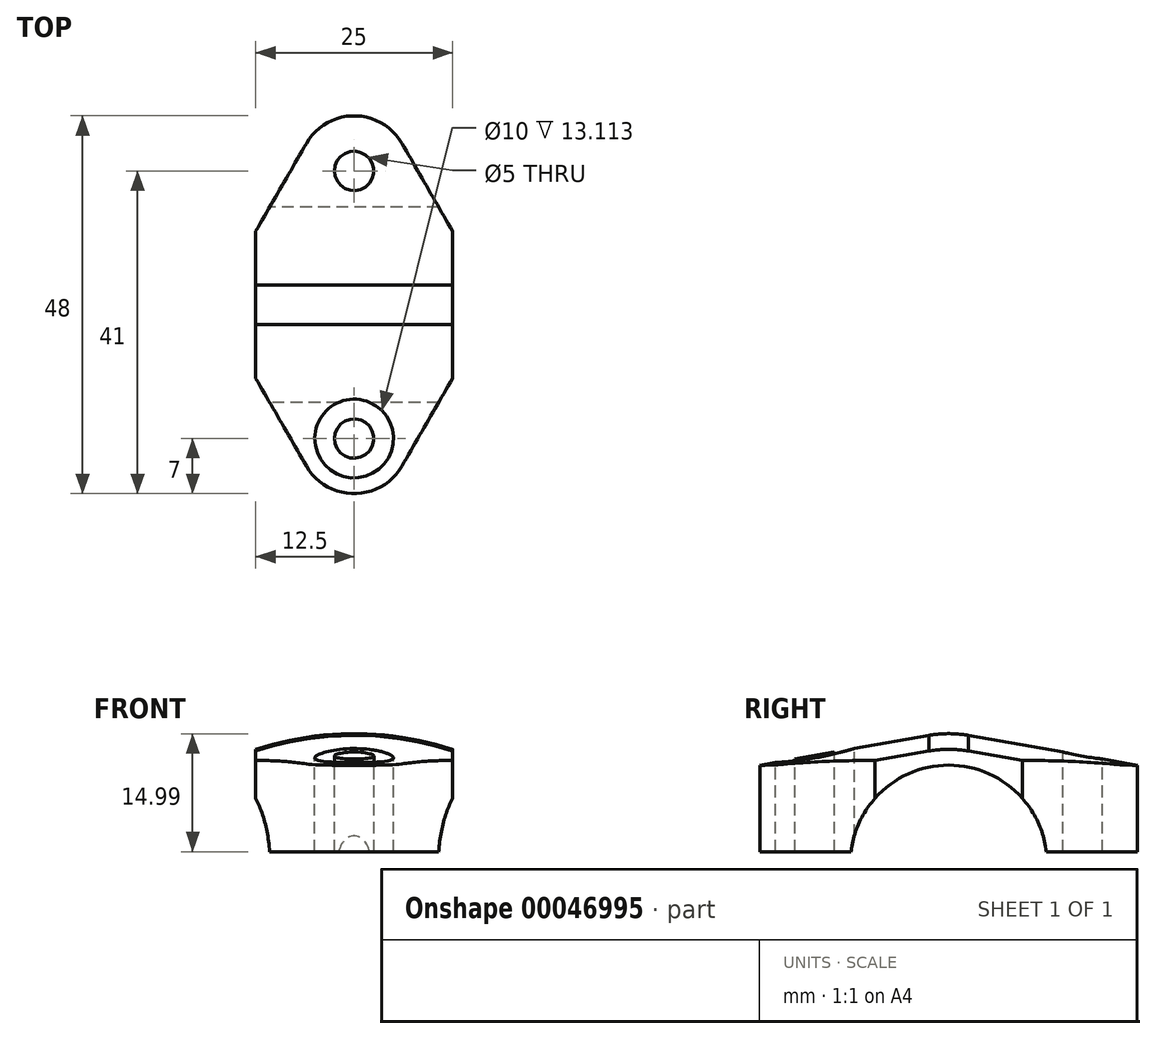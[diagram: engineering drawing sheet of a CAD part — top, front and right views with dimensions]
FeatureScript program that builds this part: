
annotation { "Feature Type Name" : "Feature", "Feature Type Description" : "" }
export const myFeature = defineFeature(function(context is Context, id is Id, definition is map)
    precondition{}
    {
        {
            var Q0;
            Q0=qCreatedBy(makeId("Right.planeOp"),FACE);
            var sketch = newSketch(context, id + "F0", { "sketchPlane" : qUnion([Q0])});
            skCircle(sketch, "E0", {"center": v(0, 0) * mm, "radius": 12.5 * mm});
            skCircle(sketch, "E1", {"center": v(0, 0) * mm, "radius": 14.5 * mm});
            skLineSegment(sketch, "E2", {"start": v(-78.22, 0) * mm, "end": v(73.33, 0) * mm, "construction": true});
            skLineSegment(sketch, "E3", {"start": v(-24, 1.5) * mm, "end": v(0, 1.5) * mm});
            skLineSegment(sketch, "E4", {"start": v(-2.52, 14.28) * mm, "end": v(-24, 10.5) * mm});
            skLineSegment(sketch, "E5", {"start": v(-24, 10.5) * mm, "end": v(-24, 1.5) * mm});
            skLineSegment(sketch, "E6", {"start": v(0, 19.52) * mm, "end": v(0, -21.8) * mm, "construction": true});
            skLineSegment(sketch, "E7.MirrorCS", {"start": v(24, 1.5) * mm, "end": v(0, 1.5) * mm});
            skLineSegment(sketch, "E8.MirrorCS", {"start": v(24, 10.5) * mm, "end": v(24, 1.5) * mm});
            skLineSegment(sketch, "E9.MirrorCS", {"start": v(2.52, 14.28) * mm, "end": v(24, 10.5) * mm});
            skSolve(sketch);
        }
        {
            var Q0;
            {var subQ0=sQuery(id+"F0.wireOp",EDGE,"E4");Q0=makeQuery(id+"F0.imprint","IMPRINT",FACE,{"disambiguationData":[TD([[makeQuery(id+"F0.imprint","IMPRINT",EDGE,{"derivedFrom":subQ0}),1.0]])]});}
            var Q1;
            {var subQ4=sQuery(id+"F0.wireOp",EDGE,"E8.MirrorCS");Q1=makeQuery(id+"F0.imprint","IMPRINT",FACE,{"disambiguationData":[TD([[makeQuery(id+"F0.imprint","IMPRINT",EDGE,{"derivedFrom":subQ4}),-1.0]])]});}
            var Q2;
            {var subQ2=sQuery(id+"F0.wireOp",EDGE,"E3");var subQ7=sQuery(id+"F0.wireOp",EDGE,"E0");var subQ8=makeQuery(id+"F0.imprint","INTERSECT",VERTEX,{"derivedFrom":[subQ7,subQ2]});Q2=makeQuery(id+"F0.imprint","IMPRINT",FACE,{"disambiguationData":[TD([[makeQuery(id+"F0.imprint","IMPRINT",EDGE,{"disambiguationData":[TD([[subQ8,1.0]])],"derivedFrom":subQ7}),-1.0]])]});}
            extrude(context, id + "F1", {"entities" : qUnion([Q0, Q1, Q2]), "endBound" : BoundingType.SYMMETRIC, "depth" : 25 * mm});
        }
        {
            var Q0;
            Q0=makeQuery(id+"F1.opExtrude","SWEPT_FACE",FACE,{"disambiguationData":[OSD([sQuery(id+"F0.wireOp",EDGE,"E5")])]});
            var sketch = newSketch(context, id + "F2", { "sketchPlane" : qUnion([Q0])});
            skArc(sketch, "E10", {"start": v(12.5, 10.5) * mm, "mid": v(0, 12.5) * mm, "end": v(-12.5, 10.5) * mm});
            skSolve(sketch);
        }
        {
            var Q0;
            Q0=makeQuery(id+"F2.imprint","IMPRINT",FACE,{"disambiguationData":[TD([[makeQuery(id+"F2.imprint","IMPRINT",EDGE,{"derivedFrom":sQuery(id+"F2.wireOp",EDGE,"E10")}),1.0]])]});
            var Q1;
            Q1=makeQuery(id+"F1.opExtrude","CAP_EDGE",EDGE,{"disambiguationData":[OSD([sQuery(id+"F0.wireOp",EDGE,"E4")])],"isStart":false});
            var Q2;
            Q2=makeQuery(id+"F1.opExtrude","CAP_EDGE",EDGE,{"disambiguationData":[OSD([sQuery(id+"F0.wireOp",EDGE,"E1")])],"isStart":false});
            var Q3;
            Q3=makeQuery(id+"F1.opExtrude","CAP_EDGE",EDGE,{"disambiguationData":[OSD([sQuery(id+"F0.wireOp",EDGE,"E9.MirrorCS")])],"isStart":false});
            sweep(context, id + "F3", {"operationType" : NewBodyOperationType.ADD, "profiles" : qUnion([Q0]), "path" : qUnion([Q1, Q2, Q3]), "keepProfileOrientation" : true});
        }
        {
            var Q0;
            Q0=makeQuery(id+"F1.opExtrude","SWEPT_FACE",FACE,{"disambiguationData":[OSD([sQuery(id+"F0.wireOp",EDGE,"E3")])]});
            cPlane(context, id + "F4", {"entities" : qUnion([Q0]), "cplaneType" : CPlaneType.OFFSET, "offset" : 30 * mm, "oppositeDirection" : true, "width" : 150 * mm, "height" : 150 * mm});
        }
        {
            var Q0;
            Q0=qCreatedBy(id+"F4.planeOp",FACE);
            var sketch = newSketch(context, id + "F5", { "sketchPlane" : qUnion([Q0])});
            skCircle(sketch, "E11", {"center": v(0, -17) * mm, "radius": 7 * mm});
            skLineSegment(sketch, "E12", {"start": v(-31.34, 0) * mm, "end": v(29.18, 0) * mm, "construction": true});
            skCircle(sketch, "E13", {"center": v(0, -17) * mm, "radius": 5 * mm});
            skCircle(sketch, "E14", {"center": v(0, -17) * mm, "radius": 2.5 * mm});
            skLineSegment(sketch, "E15", {"start": v(12.5, 24) * mm, "end": v(12.5, -24) * mm});
            skLineSegment(sketch, "E16", {"start": v(-12.5, -24) * mm, "end": v(-12.5, 24) * mm});
            skLineSegment(sketch, "E17", {"start": v(-6.06, -20.5) * mm, "end": v(-12.5, -9.35) * mm});
            skLineSegment(sketch, "E18", {"start": v(6.06, -20.5) * mm, "end": v(12.5, -9.35) * mm});
            skLineSegment(sketch, "E19", {"start": v(-12.5, -24) * mm, "end": v(12.5, -24) * mm});
            skLineSegment(sketch, "E20.MirrorCS", {"start": v(-6.06, 20.5) * mm, "end": v(-12.5, 9.35) * mm});
            skCircle(sketch, "E21.MirrorC", {"center": v(0, 17) * mm, "radius": 7 * mm});
            skCircle(sketch, "E22.MirrorC", {"center": v(0, 17) * mm, "radius": 5 * mm});
            skCircle(sketch, "E23.MirrorC", {"center": v(0, 17) * mm, "radius": 2.5 * mm});
            skLineSegment(sketch, "E24.MirrorCS", {"start": v(6.06, 20.5) * mm, "end": v(12.5, 9.35) * mm});
            skLineSegment(sketch, "E25.MirrorCS", {"start": v(-12.5, 24) * mm, "end": v(12.5, 24) * mm});
            skSolve(sketch);
        }
        {
            var Q0;
            {var subQ0=sQuery(id+"F5.wireOp",EDGE,"E17");Q0=makeQuery(id+"F5.imprint","IMPRINT",FACE,{"disambiguationData":[TD([[makeQuery(id+"F5.imprint","IMPRINT",EDGE,{"derivedFrom":subQ0}),1.0]])]});}
            var Q1;
            {var subQ0=sQuery(id+"F5.wireOp",EDGE,"E18");Q1=makeQuery(id+"F5.imprint","IMPRINT",FACE,{"disambiguationData":[TD([[makeQuery(id+"F5.imprint","IMPRINT",EDGE,{"derivedFrom":subQ0}),-1.0]])]});}
            var Q2;
            Q2=makeQuery(id+"F5.imprint","IMPRINT",FACE,{"disambiguationData":[TD([[makeQuery(id+"F5.imprint","IMPRINT",EDGE,{"derivedFrom":sQuery(id+"F5.wireOp",EDGE,"E14")}),1.0]])]});
            var Q3;
            {var subQ3=sQuery(id+"F5.wireOp",EDGE,"E24.MirrorCS");Q3=makeQuery(id+"F5.imprint","IMPRINT",FACE,{"disambiguationData":[TD([[makeQuery(id+"F5.imprint","IMPRINT",EDGE,{"derivedFrom":subQ3}),1.0]])]});}
            var Q4;
            Q4=makeQuery(id+"F5.imprint","IMPRINT",FACE,{"disambiguationData":[TD([[makeQuery(id+"F5.imprint","IMPRINT",EDGE,{"derivedFrom":sQuery(id+"F5.wireOp",EDGE,"E23.MirrorC")}),-1.0]])]});
            var Q5;
            {var subQ3=sQuery(id+"F5.wireOp",EDGE,"E20.MirrorCS");Q5=makeQuery(id+"F5.imprint","IMPRINT",FACE,{"disambiguationData":[TD([[makeQuery(id+"F5.imprint","IMPRINT",EDGE,{"derivedFrom":subQ3}),-1.0]])]});}
            var Q6;
            Q6=makeQuery(id+"F1.opExtrude","SWEPT_FACE",FACE,{"disambiguationData":[OSD([sQuery(id+"F0.wireOp",EDGE,"E7.MirrorCS")])]});
            var Q7;
            Q7=makeQuery(id+"F1.opExtrude","SWEPT_BODY",BODY,{"disambiguationData":[OSD([sQuery(id+"F0.wireOp",EDGE,"E0"),sQuery(id+"F0.wireOp",EDGE,"E1"),sQuery(id+"F0.wireOp",EDGE,"E3"),sQuery(id+"F0.wireOp",EDGE,"E4"),sQuery(id+"F0.wireOp",EDGE,"E5"),sQuery(id+"F0.wireOp",EDGE,"E7.MirrorCS"),sQuery(id+"F0.wireOp",EDGE,"E8.MirrorCS"),sQuery(id+"F0.wireOp",EDGE,"E9.MirrorCS")])]});
            extrude(context, id + "F6", {"entities" : qUnion([Q0, Q1, Q2, Q3, Q4, Q5]), "operationType" : NewBodyOperationType.REMOVE, "endBound" : BoundingType.UP_TO_SURFACE, "endBoundEntityFace" : qUnion([Q6]), "endBoundEntityBody" : qUnion([Q7]), "depth" : 25 * mm});
        }
    });
